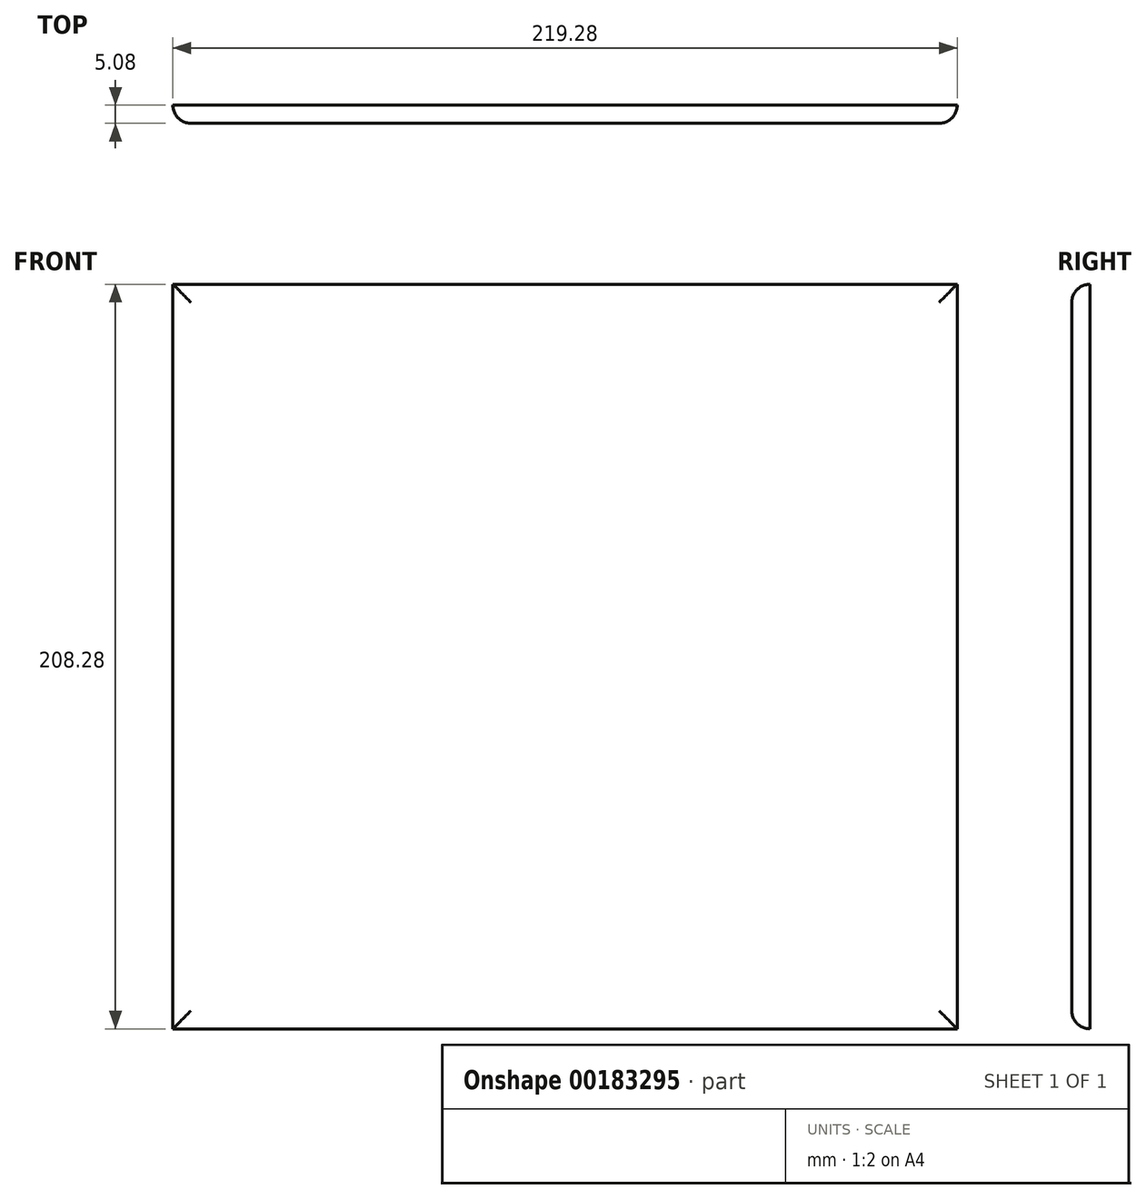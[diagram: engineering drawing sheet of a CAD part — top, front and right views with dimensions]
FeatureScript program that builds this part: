
annotation { "Feature Type Name" : "Feature", "Feature Type Description" : "" }
export const myFeature = defineFeature(function(context is Context, id is Id, definition is map)
    precondition{}
    {
        {
            var Q0;
            Q0=qCreatedBy(makeId("Front.planeOp"),FACE);
            var sketch = newSketch(context, id + "F0", { "sketchPlane" : qUnion([Q0])});
            skLineSegment(sketch, "E0.bottom", {"start": v(-82.84, 114.06) * mm, "end": v(136.44, 114.06) * mm});
            skLineSegment(sketch, "E0.top", {"start": v(-82.84, -94.22) * mm, "end": v(136.44, -94.22) * mm});
            skLineSegment(sketch, "E0.left", {"start": v(-82.84, 114.06) * mm, "end": v(-82.84, -94.22) * mm});
            skLineSegment(sketch, "E0.right", {"start": v(136.44, 114.06) * mm, "end": v(136.44, -94.22) * mm});
            skSolve(sketch);
        }
        {
            var Q0;
            Q0=makeQuery(id+"F0.imprint","IMPRINT",FACE,{"disambiguationData":[TD([[makeQuery(id+"F0.imprint","IMPRINT",EDGE,{"derivedFrom":sQuery(id+"F0.wireOp",EDGE,"E0.bottom")}),-1.0]])]});
            extrude(context, id + "F1", {"entities" : qUnion([Q0]), "endBound" : BoundingType.SYMMETRIC, "depth" : 5.08 * mm});
        }
        {
            var Q0;
            Q0=makeQuery(id+"F1.opExtrude","CAP_FACE",FACE,{"disambiguationData":[OSD([sQuery(id+"F0.wireOp",EDGE,"E0.bottom"),sQuery(id+"F0.wireOp",EDGE,"E0.top"),sQuery(id+"F0.wireOp",EDGE,"E0.left"),sQuery(id+"F0.wireOp",EDGE,"E0.right")])],"isStart":false});
            fillet(context, id + "F2", {"entities" : qUnion([Q0]), "radius" : 5.08 * mm, "tangentPropagation" : true, "allowEdgeOverflow" : false});
        }
    });
